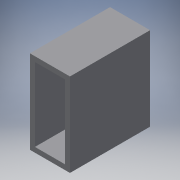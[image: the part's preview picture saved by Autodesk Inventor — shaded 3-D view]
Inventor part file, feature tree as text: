
AUTODESK INVENTOR PART (.ipt)
format: ipt  version: 2016 (Build 200138000, 138)  size: 106,496 bytes
history: native  units: in
note: dims shown in document units (in); Inventor stores cm internally (conversion verified against a paired STEP export)
features: sketch x3, extrude x2
ambient origin geometry x8: Origin, YZ Plane, XZ Plane, XY Plane, X Axis, Y Axis, Z Axis, Center Point
bodies: Solid1 (feature_tree)
feature tree (5):
  sketch  "Sketch1"  dims[d0=0.125in d1=0.125in]
  extrude  "Extrusion1"  Depth=0.125in
  extrude  "Extrusion2"  Depth=0.125in
  sketch  "Sketch2"  dims[d2=0.125in d3=0.125in]
  sketch  "Sketch3"  dims[d4=2.0in d5=1.0in d6=2.0in d7=2.0in d8=0.0in d9=1.125in d10=1.0in d11=1.0in d12=2.0in d13=0.0in]
